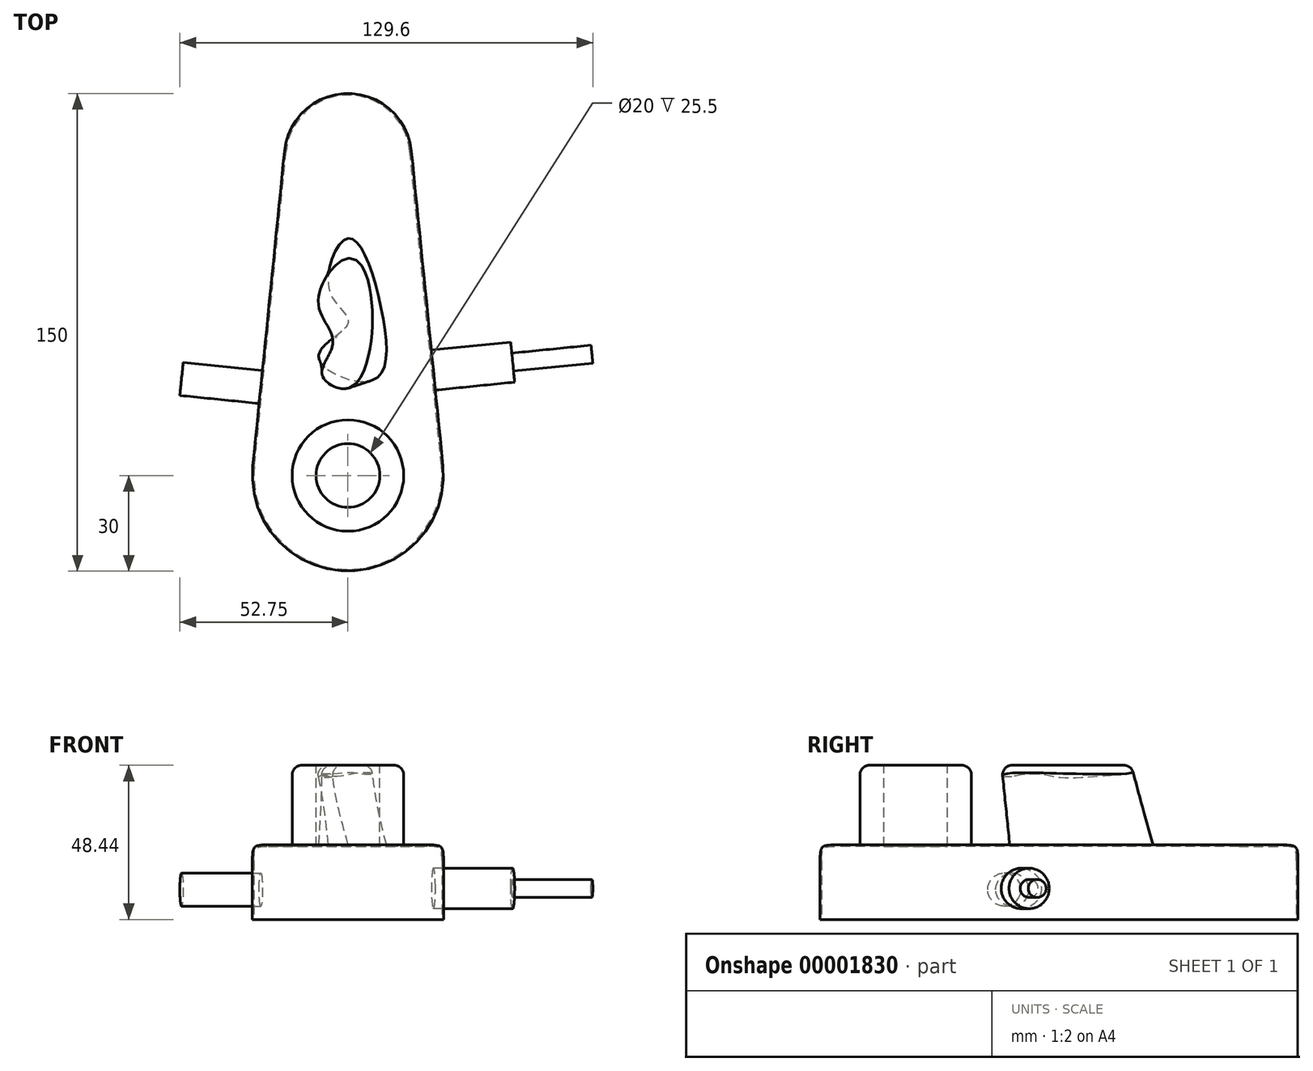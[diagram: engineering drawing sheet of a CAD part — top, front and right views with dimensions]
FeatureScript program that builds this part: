
annotation { "Feature Type Name" : "Feature", "Feature Type Description" : "" }
export const myFeature = defineFeature(function(context is Context, id is Id, definition is map)
    precondition{}
    {
        {
            var Q0;
            Q0=qCreatedBy(makeId("Top.planeOp"),FACE);
            var sketch = newSketch(context, id + "F0", { "sketchPlane" : qUnion([Q0])});
            skCircle(sketch, "E0", {"center": v(0, 0) * mm, "radius": 30 * mm});
            skCircle(sketch, "E1", {"center": v(0, 100) * mm, "radius": 20 * mm});
            skLineSegment(sketch, "E2", {"start": v(-29.85, 3) * mm, "end": v(-19.9, 102) * mm});
            skLineSegment(sketch, "E3", {"start": v(29.85, 3) * mm, "end": v(19.9, 102) * mm});
            skSolve(sketch);
        }
        {
            var Q0;
            Q0 = qSketchRegion(id + "F0", true);
            extrude(context, id + "F1", {"entities" : qUnion([Q0]), "depth" : 23.44 * mm});
        }
        {
            var Q0;
            Q0=makeQuery(id+"F1.opExtrude","CAP_EDGE",EDGE,{"disambiguationData":[OSD([sQuery(id+"F0.wireOp",EDGE,"E3")])],"isStart":false});
            fillet(context, id + "F2", {"entities" : qUnion([Q0]), "radius" : 5 * mm, "tangentPropagation" : true, "rho" : 0.7, "crossSection" : FilletCrossSection.CONIC, "allowEdgeOverflow" : false});
        }
        {
            var Q0;
            Q0=makeQuery(id+"F1.opExtrude","CAP_FACE",FACE,{"disambiguationData":[OSD([sQuery(id+"F0.wireOp",EDGE,"E0"),sQuery(id+"F0.wireOp",EDGE,"E1"),sQuery(id+"F0.wireOp",EDGE,"E2"),sQuery(id+"F0.wireOp",EDGE,"E3")])],"isStart":true});
            shell(context, id + "F3", {"entities" : qUnion([Q0]), "thickness" : 0.5 * mm});
        }
        {
            var Q0;
            Q0=makeQuery(id+"F1.opExtrude","CAP_FACE",FACE,{"disambiguationData":[OSD([sQuery(id+"F0.wireOp",EDGE,"E0"),sQuery(id+"F0.wireOp",EDGE,"E1"),sQuery(id+"F0.wireOp",EDGE,"E2"),sQuery(id+"F0.wireOp",EDGE,"E3")])],"isStart":false});
            var sketch = newSketch(context, id + "F12", { "sketchPlane" : qUnion([Q0])});
            skCircle(sketch, "E4", {"center": v(0, 0) * mm, "radius": 17.5 * mm});
            skPoint(sketch, "E5.center.orphan", {"position": v(0, 101.5) * mm});
            skSolve(sketch);
        }
        {
            var Q0;
            Q0=makeQuery(id+"F12.imprint","IMPRINT",FACE,{"disambiguationData":[TD([[makeQuery(id+"F12.imprint","IMPRINT",EDGE,{"derivedFrom":sQuery(id+"F12.wireOp",EDGE,"E4")}),1.0]])]});
            extrude(context, id + "F13", {"entities" : qUnion([Q0]), "operationType" : NewBodyOperationType.ADD, "depth" : 25 * mm});
        }
        {
            var Q0;
            Q0=makeQuery(id+"F13.opExtrude","CAP_FACE",FACE,{"disambiguationData":[OSD([sQuery(id+"F12.wireOp",EDGE,"E4")])],"isStart":false});
            var sketch = newSketch(context, id + "F4", { "sketchPlane" : qUnion([Q0])});
            skCircle(sketch, "E6", {"center": v(0, 0) * mm, "radius": 10 * mm});
            skSolve(sketch);
        }
        {
            var Q0;
            Q0=makeQuery(id+"F1.opExtrude","CAP_FACE",FACE,{"disambiguationData":[OSD([sQuery(id+"F0.wireOp",EDGE,"E0"),sQuery(id+"F0.wireOp",EDGE,"E1"),sQuery(id+"F0.wireOp",EDGE,"E2"),sQuery(id+"F0.wireOp",EDGE,"E3")])],"isStart":false});
            var sketch = newSketch(context, id + "F5", { "sketchPlane" : qUnion([Q0])});
            skFitSpline(sketch, "E7", {"points": [v(-9.17, 37.42) * mm, v(7.27, 29.82) * mm, v(10.74, 51.02) * mm, v(0, 74.47) * mm, v(-5.75, 57.94) * mm, v(0, 47.84) * mm, v(-9.17, 37.42) * mm]});
            skSolve(sketch);
        }
        {
            var Q0;
            Q0=makeQuery(id+"F13.opExtrude","CAP_FACE",FACE,{"disambiguationData":[OSD([sQuery(id+"F12.wireOp",EDGE,"E4")])],"isStart":false});
            var sketch = newSketch(context, id + "F6", { "sketchPlane" : qUnion([Q0])});
            skFitSpline(sketch, "E8", {"points": [v(-8.2, 30.96) * mm, v(-4.92, 40.7) * mm, v(-10.08, 53.45) * mm, v(0, 67.63) * mm, v(7.13, 55.77) * mm, v(0, 27.43) * mm, v(-8.2, 30.96) * mm]});
            skSolve(sketch);
        }
        {
            var Q1;
            Q1=makeQuery(id+"F6.imprint","IMPRINT",FACE,{"disambiguationData":[TD([[makeQuery(id+"F6.imprint","IMPRINT",EDGE,{"derivedFrom":sQuery(id+"F6.wireOp",EDGE,"E8")}),-1.0]])]});
            var Q2;
            Q2=makeQuery(id+"F5.imprint","IMPRINT",FACE,{"disambiguationData":[TD([[makeQuery(id+"F5.imprint","IMPRINT",EDGE,{"derivedFrom":sQuery(id+"F5.wireOp",EDGE,"E7")}),1.0]])]});
            loft(context, id + "F14", {"operationType" : NewBodyOperationType.ADD, "sheetProfilesArray" : [{ "sheetProfileEntities" : qUnion([Q1]) }, { "sheetProfileEntities" : qUnion([Q2]) }]});
        }
        {
            var Q0;
            Q0=makeQuery(id+"F13.opExtrude","CAP_EDGE",EDGE,{"disambiguationData":[OSD([sQuery(id+"F12.wireOp",EDGE,"E4")])],"isStart":false});
            var Q1;
            Q1=makeQuery(id+"F13.opExtrude","CAP_EDGE",EDGE,{"disambiguationData":[OSD([sQuery(id+"F12.wireOp",EDGE,"E4")])],"isStart":true});
            var Q2;
            Q2=makeQuery(id+"F14.opLoft","MID_CAP_EDGE",EDGE,{"disambiguationData":[OSD([sQuery(id+"F5.wireOp",EDGE,"E7"),sQuery(id+"F6.wireOp",EDGE,"E8")])],"capPos":1.0});
            var Q3;
            Q3=makeQuery(id+"F14.opLoft","MID_CAP_EDGE",EDGE,{"disambiguationData":[OSD([sQuery(id+"F6.wireOp",EDGE,"E8")])],"capPos":0.0});
            fillet(context, id + "F15", {"entities" : qUnion([Q0, Q1, Q2, Q3]), "radius" : 3 * mm, "tangentPropagation" : true, "allowEdgeOverflow" : false});
        }
        {
            var Q0;
            Q0=makeQuery(id+"F1.opExtrude","SWEPT_FACE",FACE,{"disambiguationData":[OSD([sQuery(id+"F0.wireOp",EDGE,"E2")])]});
            var sketch = newSketch(context, id + "F7", { "sketchPlane" : qUnion([Q0])});
            skCircle(sketch, "E9", {"center": v(-24.92, 9.38) * mm, "radius": 5.18 * mm});
            skSolve(sketch);
        }
        {
            var Q0;
            Q0=makeQuery(id+"F7.imprint","IMPRINT",FACE,{"disambiguationData":[TD([[makeQuery(id+"F7.imprint","IMPRINT",EDGE,{"derivedFrom":sQuery(id+"F7.wireOp",EDGE,"E9")}),1.0]])]});
            extrude(context, id + "F16", {"entities" : qUnion([Q0]), "operationType" : NewBodyOperationType.ADD, "depth" : 25 * mm});
        }
        {
            var Q0;
            Q0=makeQuery(id+"F1.opExtrude","SWEPT_FACE",FACE,{"disambiguationData":[OSD([sQuery(id+"F0.wireOp",EDGE,"E3")])]});
            var sketch = newSketch(context, id + "F8", { "sketchPlane" : qUnion([Q0])});
            skCircle(sketch, "E10", {"center": v(30.28, 9.75) * mm, "radius": 6.33 * mm});
            skSolve(sketch);
        }
        {
            var Q0;
            Q0=makeQuery(id+"F8.imprint","IMPRINT",FACE,{"disambiguationData":[TD([[makeQuery(id+"F8.imprint","IMPRINT",EDGE,{"derivedFrom":sQuery(id+"F8.wireOp",EDGE,"E10")}),1.0]])]});
            extrude(context, id + "F9", {"entities" : qUnion([Q0]), "operationType" : NewBodyOperationType.ADD, "depth" : 25 * mm});
        }
        {
            var Q0;
            Q0=makeQuery(id+"F4.imprint","IMPRINT",FACE,{"disambiguationData":[TD([[makeQuery(id+"F4.imprint","IMPRINT",EDGE,{"derivedFrom":sQuery(id+"F4.wireOp",EDGE,"E6")}),1.0]])]});
            extrude(context, id + "F17", {"entities" : qUnion([Q0]), "operationType" : NewBodyOperationType.REMOVE, "endBound" : BoundingType.UP_TO_NEXT, "oppositeDirection" : true, "depth" : 25 * mm});
        }
        {
            var Q0;
            Q0=makeQuery(id+"F9.opExtrude","CAP_FACE",FACE,{"disambiguationData":[OSD([sQuery(id+"F8.wireOp",EDGE,"E10")])],"isStart":false});
            var sketch = newSketch(context, id + "F10", { "sketchPlane" : qUnion([Q0])});
            skCircle(sketch, "E11", {"center": v(30.28, 9.75) * mm, "radius": 2.83 * mm});
            skSolve(sketch);
        }
        {
            var Q0;
            Q0=makeQuery(id+"F10.imprint","IMPRINT",FACE,{"disambiguationData":[TD([[makeQuery(id+"F10.imprint","IMPRINT",EDGE,{"derivedFrom":sQuery(id+"F10.wireOp",EDGE,"E11")}),1.0]])]});
            extrude(context, id + "F11", {"entities" : qUnion([Q0]), "operationType" : NewBodyOperationType.ADD, "depth" : 25 * mm});
        }
    });
